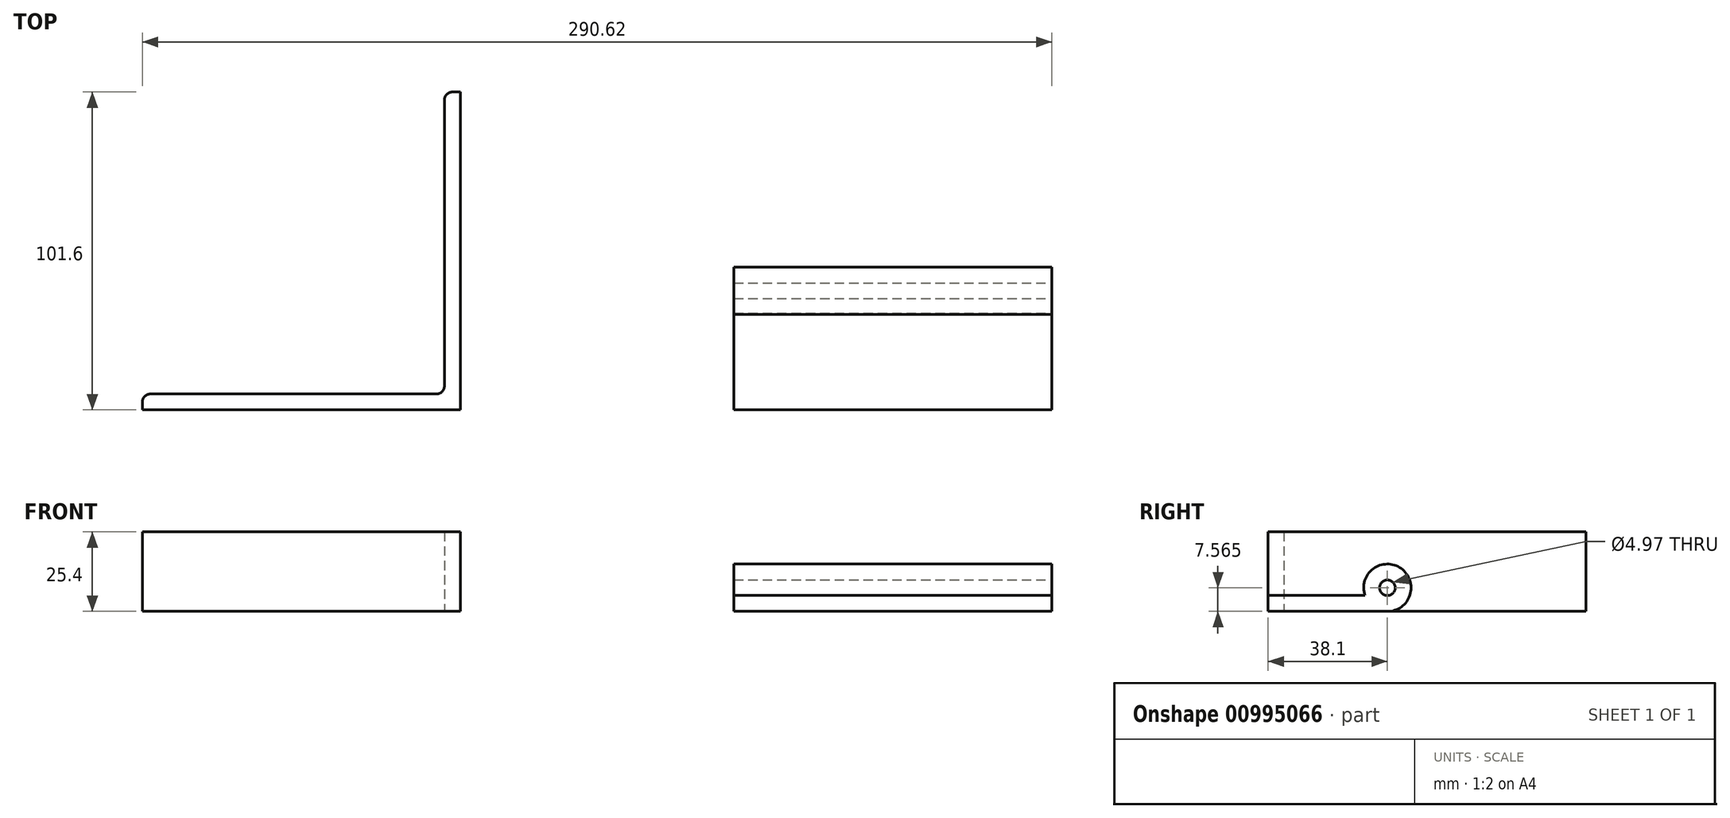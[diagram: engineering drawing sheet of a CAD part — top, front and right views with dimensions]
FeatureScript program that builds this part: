
annotation { "Feature Type Name" : "Feature", "Feature Type Description" : "" }
export const myFeature = defineFeature(function(context is Context, id is Id, definition is map)
    precondition{}
    {
        {
            var Q0;
            Q0=qCreatedBy(makeId("Top.planeOp"),FACE);
            var sketch = newSketch(context, id + "F0", { "sketchPlane" : qUnion([Q0])});
            skLineSegment(sketch, "E0.bottom", {"start": v(0, 0) * mm, "end": v(101.6, 0) * mm});
            skLineSegment(sketch, "E0.top", {"start": v(0, 38.1) * mm, "end": v(101.6, 38.1) * mm});
            skLineSegment(sketch, "E0.left", {"start": v(0, 0) * mm, "end": v(0, 38.1) * mm});
            skLineSegment(sketch, "E0.right", {"start": v(101.6, 0) * mm, "end": v(101.6, 38.1) * mm});
            skSolve(sketch);
        }
        {
            var Q0;
            Q0=makeQuery(id+"F0.imprint","IMPRINT",FACE,{"disambiguationData":[TD([[makeQuery(id+"F0.imprint","IMPRINT",EDGE,{"derivedFrom":sQuery(id+"F0.wireOp",EDGE,"E0.bottom")}),1.0]])]});
            extrude(context, id + "F1", {"entities" : qUnion([Q0]), "depth" : 5.08 * mm, "offsetDistance" : 25.4 * mm});
        }
        {
            var Q0;
            Q0=makeQuery(id+"F1.opExtrude","SWEPT_FACE",FACE,{"disambiguationData":[OSD([sQuery(id+"F0.wireOp",EDGE,"E0.right")])]});
            var sketch = newSketch(context, id + "F2", { "sketchPlane" : qUnion([Q0])});
            skCircle(sketch, "E1", {"center": v(38.1, 7.57) * mm, "radius": 7.57 * mm});
            skCircle(sketch, "E2", {"center": v(38.1, 7.57) * mm, "radius": 2.49 * mm});
            skSolve(sketch);
        }
        {
            var Q0;
            {var subQ5=sQuery(id+"F2.wireOp",EDGE,"E2");Q0=makeQuery(id+"F2.imprint","IMPRINT",FACE,{"disambiguationData":[TD([[makeQuery(id+"F2.imprint","IMPRINT",EDGE,{"derivedFrom":subQ5}),-1.0]])]});}
            var Q1;
            {var subQ1=sQuery(id+"F0.wireOp",EDGE,"E0.right");var subQ2=makeQuery(id+"F1.opExtrude","SWEPT_EDGE",EDGE,{"disambiguationData":[OSD([sQuery(id+"F0.wireOp",EDGE,"E0.top"),subQ1])]});Q1=makeQuery(id+"F2.imprint","IMPRINT",FACE,{"disambiguationData":[TD([[makeQuery(id+"F2.imprint","IMPRINT",EDGE,{"derivedFrom":subQ2}),-1.0]])]});}
            extrude(context, id + "F3", {"entities" : qUnion([Q0, Q1]), "operationType" : NewBodyOperationType.ADD, "oppositeDirection" : true, "depth" : 101.6 * mm, "offsetDistance" : 25.4 * mm});
        }
        {
            var Q0;
            Q0=qCreatedBy(makeId("Top.planeOp"),FACE);
            var sketch = newSketch(context, id + "F4", { "sketchPlane" : qUnion([Q0])});
            skLineSegment(sketch, "E3.bottom", {"start": v(-87.42, 0) * mm, "end": v(-189.02, 0) * mm});
            skLineSegment(sketch, "E3.top", {"start": v(-87.42, 101.6) * mm, "end": v(-89.96, 101.6) * mm});
            skLineSegment(sketch, "E3.left", {"start": v(-87.42, 0) * mm, "end": v(-87.42, 101.6) * mm});
            skLineSegment(sketch, "E3.right", {"start": v(-189.02, 0) * mm, "end": v(-189.02, 2.54) * mm});
            skLineSegment(sketch, "E4.top", {"start": v(-186.48, 5.08) * mm, "end": v(-95.04, 5.08) * mm});
            skLineSegment(sketch, "E4.right", {"start": v(-92.5, 99.06) * mm, "end": v(-92.5, 7.62) * mm});
            skArc(sketch, "E5.filletArc", {"start": v(-186.48, 5.08) * mm, "mid": v(-188.27, 4.34) * mm, "end": v(-189.02, 2.54) * mm});
            skArc(sketch, "E6.filletArc", {"start": v(-89.96, 101.6) * mm, "mid": v(-91.75, 100.86) * mm, "end": v(-92.5, 99.06) * mm});
            skPoint(sketch, "E7.visualSharp", {"position": v(-92.5, 5.08) * mm});
            skArc(sketch, "E7.filletArc", {"start": v(-95.04, 5.08) * mm, "mid": v(-93.24, 5.82) * mm, "end": v(-92.5, 7.62) * mm});
            skSolve(sketch);
        }
        {
            var Q0;
            Q0=makeQuery(id+"F4.imprint","IMPRINT",FACE,{"disambiguationData":[TD([[makeQuery(id+"F4.imprint","IMPRINT",EDGE,{"derivedFrom":sQuery(id+"F4.wireOp",EDGE,"E3.bottom")}),-1.0]])]});
            extrude(context, id + "F5", {"entities" : qUnion([Q0]), "depth" : 25.4 * mm, "offsetDistance" : 25.4 * mm});
        }
    });
